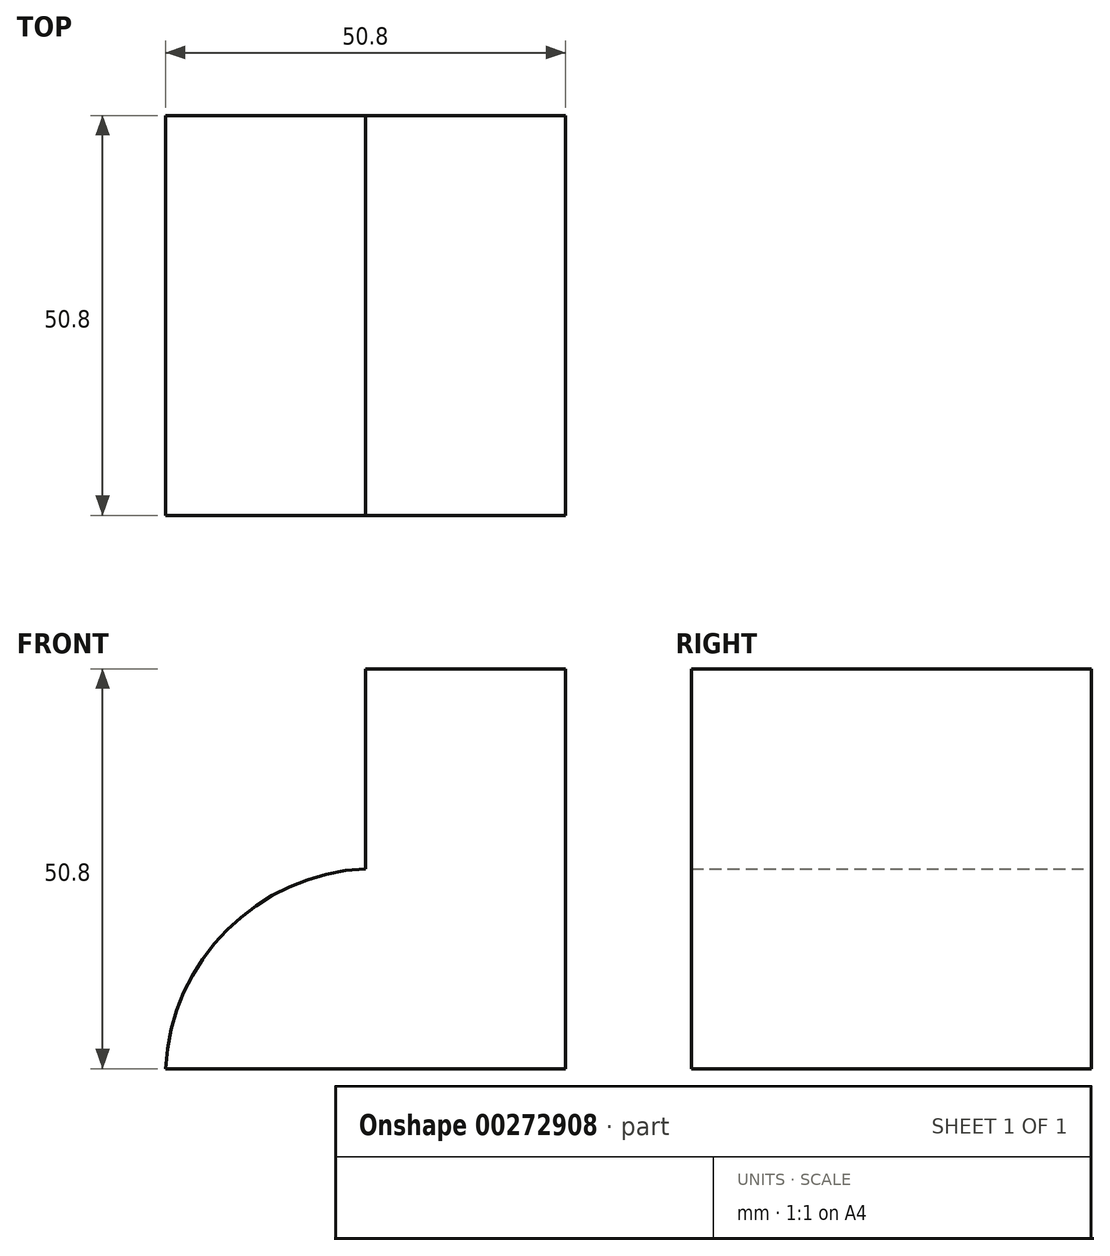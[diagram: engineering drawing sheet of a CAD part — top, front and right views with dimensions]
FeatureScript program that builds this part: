
annotation { "Feature Type Name" : "Feature", "Feature Type Description" : "" }
export const myFeature = defineFeature(function(context is Context, id is Id, definition is map)
    precondition{}
    {
        {
            var Q0;
            Q0=qCreatedBy(makeId("Front.planeOp"),FACE);
            var sketch = newSketch(context, id + "F0", { "sketchPlane" : qUnion([Q0])});
            skLineSegment(sketch, "E0", {"start": v(0, 0) * mm, "end": v(-50.8, 0) * mm});
            skLineSegment(sketch, "E1", {"start": v(0, 0) * mm, "end": v(0, 50.8) * mm});
            skLineSegment(sketch, "E2", {"start": v(0, 50.8) * mm, "end": v(-25.4, 50.8) * mm});
            skLineSegment(sketch, "E3", {"start": v(-25.4, 50.8) * mm, "end": v(-25.4, 25.4) * mm});
            skArc(sketch, "E4", {"start": v(-25.4, 25.4) * mm, "mid": v(-43.02, 17.62) * mm, "end": v(-50.8, 0) * mm});
            skSolve(sketch);
        }
        {
            var Q0;
            Q0 = qSketchRegion(id + "F0", true);
            extrude(context, id + "F1", {"entities" : qUnion([Q0]), "depth" : 50.8 * mm});
        }
    });
